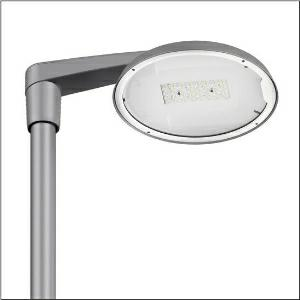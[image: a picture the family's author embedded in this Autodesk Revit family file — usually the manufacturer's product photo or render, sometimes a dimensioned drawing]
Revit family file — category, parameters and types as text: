
# Revit family: dl_50_iq_mini___st0_5a_5xa248b31f08ge_aa81
name_source: partatom
category: Lighting Fixtures
units: mm (PartAtom-declared; Revit-internal decimal feet)

## family parameters
Cut with Voids When Loaded = No
Host = Face
Light Source = No
Part Type = Normal
Room Calculation Point = No
Round Connector Dimension = Use Diameter
Shared = No

## types (1)
- --- (1 x LED, 5190 lm, 32.7 W, 3000K)
    Apparent Load = 33 VA
    CIE Flux Codes = 41 75 97 100 100
    Color Rendering = 70
    Color Temperature = 3000K
    Default Elevation = 1800 mm
    Description = DL 50 iQ mini, mast luminaire, primary light control with lens, of PMMA, primary optical cover: cover, of toughened safety glass, transparent, light distribution: ST0.5a, light emission: direct distribution, primary light characteristic: asymmetric, installation type: side-entry, post-top, LED, High Power LED, rated luminous flux: 5.190lm, luminous efficacy: 159lm/W, light colour: 730, colour temperature: 3000K, control gear: iQ Street-Remote, control: optimised constant luminous flux control (CLO 2.0), Desk-Remote (wireless, voltage-free reading and setting of iQ features in the workshop via application-optimized NFC function/RFID function), Light-Fading, Smart-Wire, Night-Set, Lumen-Switch, Temp-Guard, Auto-Match, Street-Remote, mains connection: 230..240V, AC, 50/60Hz, connection cable pre-assembled, cable length: 6,5m, start of lifetime: 33W, end of service life: 34W, reduction: 16W, luminaire housing, of diecast aluminium, powder-coated, SITECO metallic grey (DB 702S), inclination adjustable: 0°, 5°, 10° (post-top) | 0°, -5°, -10°, -15° (side-entry), please order mast post-top element or mast side-entry element separately, diameter: 500mm, height: 115mm, post-top: for spigot size d x l = 76 x 100mm; with reducer (optional accessory) 60 x 100mm | side-entry: for spigot size d x l = 60 x 100mm; with reducer (optional accessory) 42 x 100mm, mounting height: 4..6m, protection rating (complete): IP66, insulation class (complete): insulation class II (safety insulation), certification: CE, ENEC, ENEC+, VDE, impact resistance: IK08, permissible operating ambient temperature for outdoor applications: -25..+40°C, standard-compliant lighting for roads and squares, packaging unit: 1 piece

Light Distribution: ST0.5a
    Height = 115 mm
    Lamp = 1 x LED
    Lamp Light Flux = 5190 lm
    Lamp Power = 32.7 W
    Lamp count = 1
    Length = 500 mm
    Luminous efficacy = 159 lm/W
    Manufacturer = Siteco
    ModVariant = No
    Model = 5XA248B31F08GE
    Number of Poles = 1
    OnlyDefault = Yes
    Power Factor = 1
    Product Name = DL 50 iQ mini | ST0.5a
    Product group = mast luminaire | pylon top
    ProductGroupID = 6100
    Protection Class = Protection class II
    Protection Degree = IP 66
    RLX_Detail_Level = 1
    RLX_Emergency_Light_Flux = 0 lm
    RLX_Emergency_Type = 0
    RLX_Emergency_Type_DB = No
    RlxData = <blob elided: 126897 chars, md5=b6449af4>
    Socket = socket
    Standby Power = 0 W
    System Light Flux = 5190 lm
    System Power = 33 W
    Type Comments = factory setting: luminous flux: 100 % | dim-lin: 254 | 340 mA
    Type Image = l_1251794.jpg
    URL = http://relux.com
    VarID = @adj_142795
    Voltage = 0 V
    Weight = 0.00 kg
    Width = 0 mm  [stored 0 ft]

note: [stored X ft] marks values corroborated as IEEE doubles in the binary element streams (Revit-internal decimal feet)

## geometry (parser evidence)
native form markers: Blend x4, Sweep x10
no freeform markers — native parametric forms only
